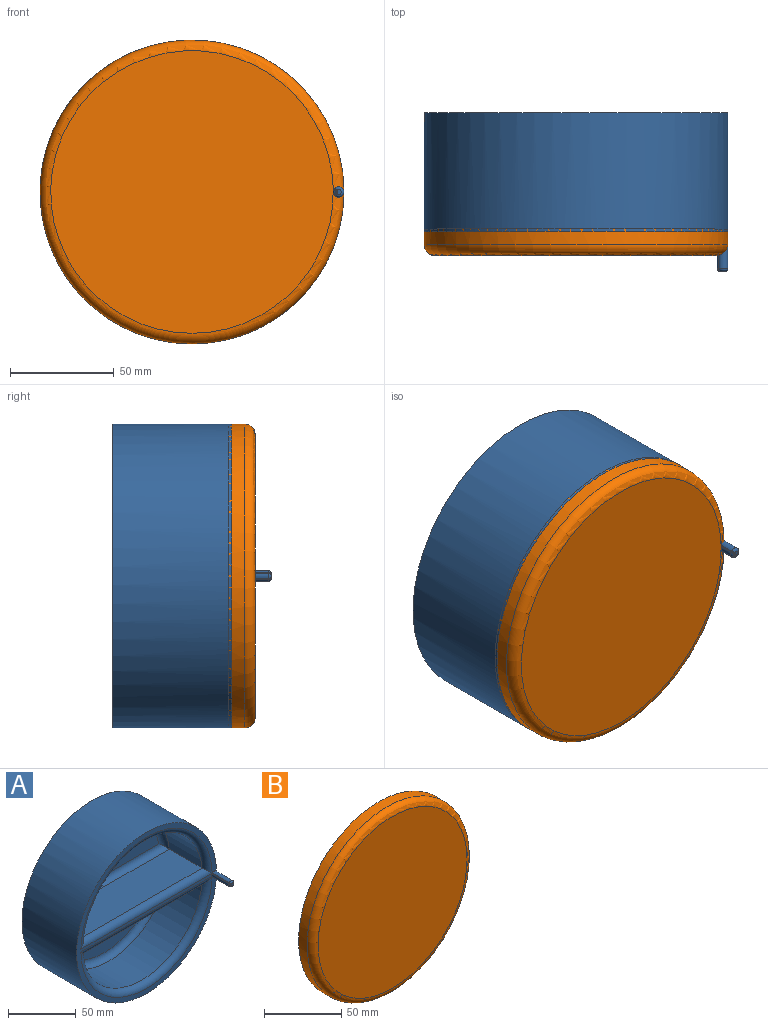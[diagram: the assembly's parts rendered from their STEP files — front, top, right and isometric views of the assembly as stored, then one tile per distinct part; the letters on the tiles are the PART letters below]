
ASSEMBLY  parts=2 mates=1
PART A: 29 faces, bbox 156.2x76.2x156.3 mm
  f0: cylinder r=63.5mm len=126.36mm, axis (0,1,0), area 6404.3mm2, adj f4,f9,f14
  f1: cylinder r=63.5mm len=126.36mm, axis (0,1,0), area 6404.3mm2, adj f2,f12,f15
  f2: plane 126.36x34.29mm, normal (0,0,1), area 4333mm2, adj f1,f11,f16
  f3: cylinder r=73.03mm len=146.05mm, axis (0,1,0), area 26222.1mm2, adj f5,f6
  f4: plane 126.36x34.29mm, normal (0,0,-1), area 4333mm2, adj f0,f10,f13
  f5: plane 146.05x146.05mm, normal (0,-1,0), area 2305.6mm2, adj f3,f13,f14,f15,f16,f17,f20
  f6: plane 146.05x146.05mm, normal (0,1,0), area 16753mm2, adj f3
  f7: plane 114.58x46.99mm, normal (0,-1,0), area 4034.1mm2, adj f11,f12
  f8: plane 114.58x46.99mm, normal (0,-1,0), area 4034.1mm2, adj f9,f10
  f9: torus R=58.42mm, axis (0,-1,0), area 1414.3mm2, adj f0,f8,f10
  f10: cylinder r=5.08mm len=126.36mm, axis (1,0,0), area 974.8mm2, adj f4,f8,f9
  f11: cylinder r=5.08mm len=126.36mm, axis (-1,0,0), area 974.8mm2, adj f2,f7,f12
  f12: torus R=58.42mm, axis (0,-1,0), area 1414.3mm2, adj f1,f7,f11
  f13: cylinder r=5.08mm len=137.14mm, axis (-1,0,0), area 1040.1mm2, adj f4,f5,f14,f21
  f14: torus R=68.58mm, axis (0,-1,0), area 1566.2mm2, adj f0,f5,f13,f22
  f15: torus R=68.58mm, axis (0,-1,0), area 1566.2mm2, adj f1,f5,f16,f18
  f16: cylinder r=5.08mm len=137.14mm, axis (1,0,0), area 1040.1mm2, adj f2,f5,f15,f19
  f17: cylinder r=2.54mm len=17.78mm, axis (0,1,0), area 219.6mm2, adj f5,f18,f22,f24
  f18: cylinder r=68.58mm len=17.78mm, axis (0,1,0), area 6.9mm2, adj f15,f17,f19,f25
  f19: plane 17.78x0.28mm, normal (0,0,1), area 5mm2, adj f16,f18,f20,f27
  f20: cylinder r=2.54mm len=17.78mm, axis (0,1,0), area 47.3mm2, adj f5,f19,f21,f28
  f21: plane 17.78x0.28mm, normal (0,0,-1), area 5mm2, adj f13,f20,f22,f27
  f22: cylinder r=68.58mm len=17.78mm, axis (0,1,0), area 6.9mm2, adj f14,f17,f21,f26
  f23: plane 2.54x1.91mm, normal (0,-1,0), area 4.1mm2, adj f24,f25,f26
  f24: torus R=1.27mm, axis (0,-1,0), area 19.5mm2, adj f17,f23,f25,f26
  f25: torus R=69.85mm, axis (0,-1,0), area 1.3mm2, adj f18,f23,f24,f27
  f26: torus R=69.85mm, axis (0,-1,0), area 1.3mm2, adj f22,f23,f24,f27
  f27: cylinder r=1.27mm len=2.54mm, axis (1,0,0), area 1.8mm2, adj f19,f21,f25,f26,f28
  f28: torus R=1.27mm, axis (0,-1,0), area 3.3mm2, adj f20,f27
PART B: 6 faces, bbox 158.1x12.7x158.1 mm
  f0: cylinder r=73.03mm len=146.05mm, axis (0,1,0), area 3496.3mm2, adj f2,f3
  f1: plane 135.89x135.89mm, normal (0,-1,0), area 14503.2mm2, adj f3
  f2: plane 146.05x146.05mm, normal (0,1,0), area 16732.7mm2, adj f0,f4
  f3: torus R=67.95mm, axis (0,-1,0), area 3568.7mm2, adj f0,f1
  f4: cylinder r=2.54mm len=5.08mm, axis (0,-1,0), area 0.4mm2, adj f2,f5
  f5: plane 5.08x5.08mm, normal (0,1,0), area 20.3mm2, adj f4
PLACE A t=(-73.88,-2.44,3.16)mm
PLACE B t=(-73.88,-58.32,3.16)mm
MATE revolute B.f4 <-> A.f17  axis (0,1,0) through (-3.39,-58.32,3.16)mm
